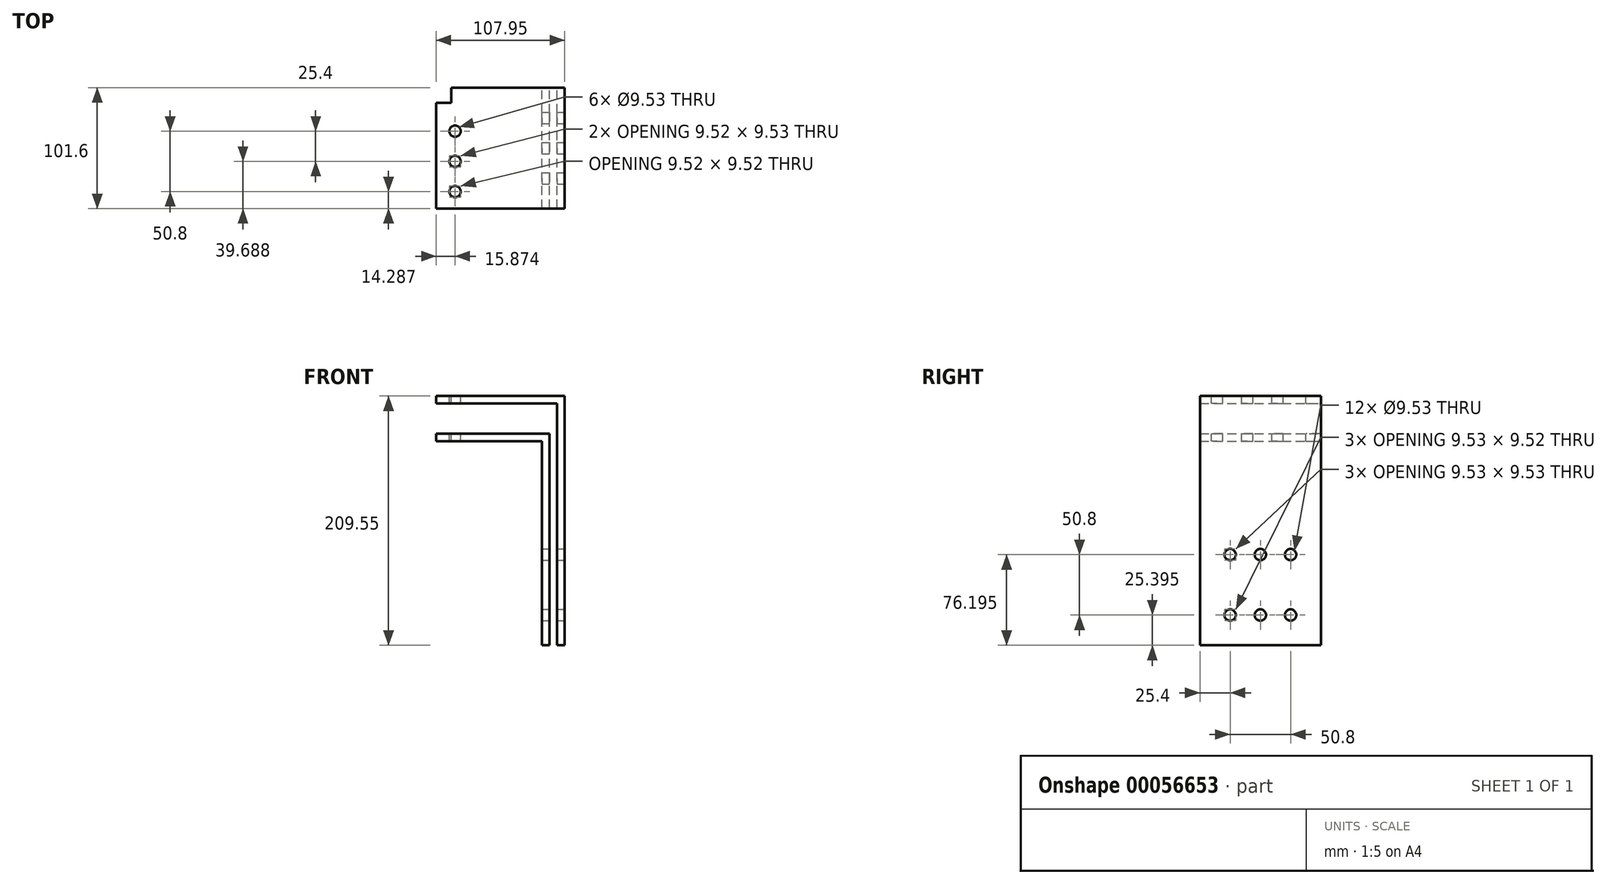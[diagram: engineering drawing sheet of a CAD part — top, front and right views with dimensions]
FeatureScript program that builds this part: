
annotation { "Feature Type Name" : "Feature", "Feature Type Description" : "" }
export const myFeature = defineFeature(function(context is Context, id is Id, definition is map)
    precondition{}
    {
        {
            var Q0;
            Q0=qCreatedBy(makeId("Front.planeOp"),FACE);
            var sketch = newSketch(context, id + "F0", { "sketchPlane" : qUnion([Q0])});
            skLineSegment(sketch, "E0", {"start": v(-138.97, 109.27) * mm, "end": v(-43.72, 109.27) * mm});
            skLineSegment(sketch, "E1", {"start": v(-43.72, 109.27) * mm, "end": v(-43.72, -68.53) * mm});
            skLineSegment(sketch, "E2", {"start": v(-50.07, 102.92) * mm, "end": v(-138.97, 102.92) * mm});
            skLineSegment(sketch, "E3", {"start": v(-37.37, 134.67) * mm, "end": v(-138.97, 134.67) * mm});
            skLineSegment(sketch, "E4", {"start": v(-138.97, 134.67) * mm, "end": v(-138.97, 141.02) * mm});
            skLineSegment(sketch, "E5", {"start": v(-138.97, 141.02) * mm, "end": v(-31.02, 141.02) * mm});
            skLineSegment(sketch, "E6", {"start": v(-31.02, 141.02) * mm, "end": v(-31.02, -68.53) * mm});
            skLineSegment(sketch, "E7", {"start": v(-50.07, -68.53) * mm, "end": v(-43.72, -68.53) * mm});
            skLineSegment(sketch, "E8.trimOffspring", {"start": v(-50.07, -68.53) * mm, "end": v(-50.07, 102.92) * mm});
            skLineSegment(sketch, "E9.trimOffspring", {"start": v(-37.37, -68.53) * mm, "end": v(-37.37, 134.67) * mm});
            skLineSegment(sketch, "E10.trimOffspring", {"start": v(-37.37, -68.53) * mm, "end": v(-31.02, -68.53) * mm});
            skLineSegment(sketch, "E11", {"start": v(-138.97, 109.27) * mm, "end": v(-138.97, 102.92) * mm});
            skSolve(sketch);
        }
        {
            var Q0;
            Q0 = qSketchRegion(id + "F0", true);
            extrude(context, id + "F1", {"entities" : qUnion([Q0]), "endBound" : BoundingType.SYMMETRIC, "depth" : 101.6 * mm});
        }
        {
            var Q0;
            Q0=makeQuery(id+"F1.opExtrude","SWEPT_FACE",FACE,{"disambiguationData":[OSD([sQuery(id+"F0.wireOp",EDGE,"E6")])]});
            var sketch = newSketch(context, id + "F2", { "sketchPlane" : qUnion([Q0])});
            skCircle(sketch, "E12", {"center": v(-25.4, -43.13) * mm, "radius": 4.76 * mm});
            skCircle(sketch, "E13.0.1.0", {"center": v(-25.4, 7.67) * mm, "radius": 4.76 * mm});
            skCircle(sketch, "E13.1.0.0", {"center": v(0, -43.13) * mm, "radius": 4.76 * mm});
            skCircle(sketch, "E13.1.1.0", {"center": v(0, 7.67) * mm, "radius": 4.76 * mm});
            skCircle(sketch, "E13.2.0.0", {"center": v(25.4, -43.13) * mm, "radius": 4.76 * mm});
            skCircle(sketch, "E13.2.1.0", {"center": v(25.4, 7.67) * mm, "radius": 4.76 * mm});
            skLineSegment(sketch, "E13.direction1", {"start": v(-25.4, -43.13) * mm, "end": v(0, -43.13) * mm, "construction": true});
            skLineSegment(sketch, "E13.direction2", {"start": v(-25.4, -43.13) * mm, "end": v(-25.4, 7.67) * mm, "construction": true});
            skSolve(sketch);
        }
        {
            var Q0;
            Q0 = qSketchRegion(id + "F2", true);
            extrude(context, id + "F3", {"entities" : qUnion([Q0]), "operationType" : NewBodyOperationType.REMOVE, "endBound" : BoundingType.THROUGH_ALL, "oppositeDirection" : true, "depth" : 25.4 * mm});
        }
        {
            var Q0;
            Q0=makeQuery(id+"F1.opExtrude","SWEPT_FACE",FACE,{"disambiguationData":[OSD([sQuery(id+"F0.wireOp",EDGE,"E5")])]});
            var sketch = newSketch(context, id + "F4", { "sketchPlane" : qUnion([Q0])});
            skCircle(sketch, "E14", {"center": v(-123.1, -36.51) * mm, "radius": 4.76 * mm});
            skCircle(sketch, "E15.0.1.0", {"center": v(-123.1, -11.11) * mm, "radius": 4.76 * mm});
            skCircle(sketch, "E15.0.2.0", {"center": v(-123.1, 14.29) * mm, "radius": 4.76 * mm});
            skLineSegment(sketch, "E15.direction1", {"start": v(-123.1, -36.51) * mm, "end": v(-97.7, -36.51) * mm, "construction": true});
            skLineSegment(sketch, "E15.direction2", {"start": v(-123.1, -36.51) * mm, "end": v(-123.1, -11.11) * mm, "construction": true});
            skLineSegment(sketch, "E16.bottom", {"start": v(-138.97, 50.8) * mm, "end": v(-126.27, 50.8) * mm});
            skLineSegment(sketch, "E16.top", {"start": v(-138.97, 38.1) * mm, "end": v(-126.27, 38.1) * mm});
            skLineSegment(sketch, "E16.left", {"start": v(-138.97, 50.8) * mm, "end": v(-138.97, 38.1) * mm});
            skLineSegment(sketch, "E16.right", {"start": v(-126.27, 50.8) * mm, "end": v(-126.27, 38.1) * mm});
            skSolve(sketch);
        }
        {
            var Q0;
            Q0 = qSketchRegion(id + "F4", true);
            extrude(context, id + "F5", {"entities" : qUnion([Q0]), "operationType" : NewBodyOperationType.REMOVE, "endBound" : BoundingType.THROUGH_ALL, "oppositeDirection" : true, "depth" : 25.4 * mm});
        }
    });
